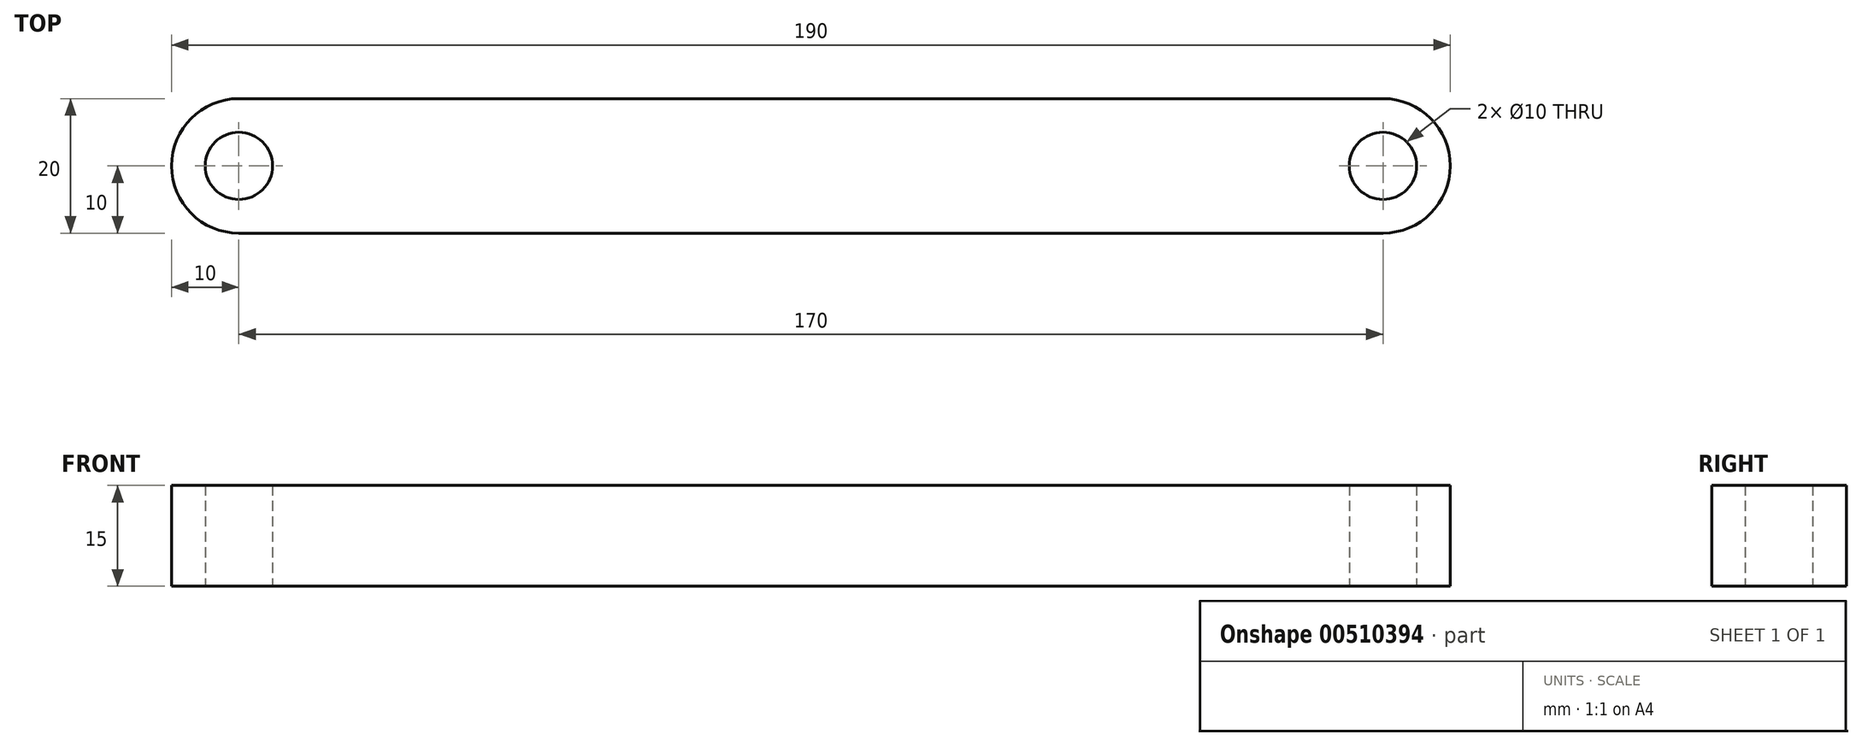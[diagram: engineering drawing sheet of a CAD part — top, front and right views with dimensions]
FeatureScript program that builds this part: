
annotation { "Feature Type Name" : "Feature", "Feature Type Description" : "" }
export const myFeature = defineFeature(function(context is Context, id is Id, definition is map)
    precondition{}
    {
        {
            var Q0;
            Q0=qCreatedBy(makeId("Top.planeOp"),FACE);
            var sketch = newSketch(context, id + "F0", { "sketchPlane" : qUnion([Q0])});
            skLineSegment(sketch, "E0.bottom", {"start": v(-85, 10) * mm, "end": v(85, 10) * mm});
            skLineSegment(sketch, "E0.top", {"start": v(-85, -10) * mm, "end": v(85, -10) * mm});
            skPoint(sketch, "E0.middle", {"position": v(0, 0) * mm});
            skArc(sketch, "E1", {"start": v(-85, 10) * mm, "mid": v(-95, 0) * mm, "end": v(-85, -10) * mm});
            skCircle(sketch, "E2", {"center": v(-85, 0) * mm, "radius": 5 * mm});
            skCircle(sketch, "E3", {"center": v(85, 0) * mm, "radius": 5 * mm});
            skArc(sketch, "E4", {"start": v(85, -10) * mm, "mid": v(95, 0) * mm, "end": v(85, 10) * mm});
            skSolve(sketch);
        }
        {
            var Q0;
            Q0=makeQuery(id+"F0.imprint","IMPRINT",FACE,{"disambiguationData":[TD([[makeQuery(id+"F0.imprint","IMPRINT",EDGE,{"derivedFrom":sQuery(id+"F0.wireOp",EDGE,"E0.bottom")}),-1.0]])]});
            extrude(context, id + "F1", {"entities" : qUnion([Q0]), "endBound" : BoundingType.SYMMETRIC, "depth" : 15 * mm});
        }
    });
